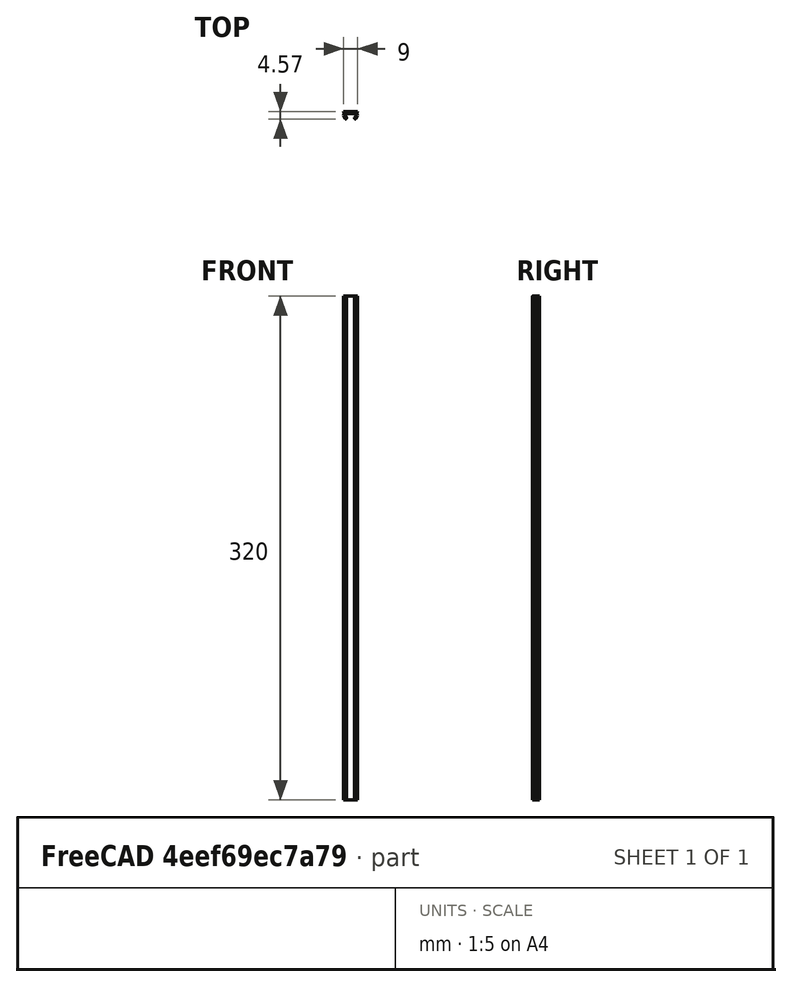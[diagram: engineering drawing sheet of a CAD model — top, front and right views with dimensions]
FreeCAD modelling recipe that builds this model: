
FCSTD DOCUMENT  (FreeCAD 0.17R13387 (Git))
Label: Strip_finishing_channel_8_Y
License: All rights reserved
LicenseURL: http://en.wikipedia.org/wiki/All_rights_reserved
objects: Sketcher::SketchObject×1, PartDesign::Pad×1, PartDesign::Body×1
note: 4 computed .brp shape members not serialized (recipe doc carries the construction recipe); baked Part::Feature solids carry a one-line shape summary decoded from their .brp

FEATURE [Sketcher::SketchObject] Sketch
  MapMode = 5
  Support = -> [XY_Plane]
  sketch-geometry (16):
    g0: LineSegment StartX=-4.5 StartY=4.3 StartZ=0 EndX=4.5 EndY=4.3 EndZ=0
    g1: LineSegment StartX=4.5 StartY=4.3 StartZ=0 EndX=4.5 EndY=4 EndZ=0
    g2: LineSegment StartX=4.5 StartY=4 StartZ=0 EndX=3.9 EndY=4 EndZ=0
    g3: LineSegment StartX=3.9 StartY=4 StartZ=0 EndX=4.5 EndY=2 EndZ=0
    g4: LineSegment StartX=4.5 StartY=2 StartZ=0 EndX=3.44197 EndY=0 EndZ=0
    g5: LineSegment StartX=2.55803 StartY=0.467615 StartZ=0 EndX=3.36869 EndY=2 EndZ=0
    g6: LineSegment StartX=3.36869 StartY=2 StartZ=0 EndX=3 EndY=3.22897 EndZ=0
    g7: LineSegment StartX=-3 StartY=3.22897 StartZ=0 EndX=-3.36869 EndY=2 EndZ=0
    g8: LineSegment StartX=-3.36869 StartY=2 StartZ=0 EndX=-2.55803 EndY=0.467615 EndZ=0
    g9: LineSegment StartX=-3.44197 StartY=0 StartZ=0 EndX=-4.5 EndY=2 EndZ=0
    g10: LineSegment StartX=-4.5 StartY=2 StartZ=0 EndX=-3.9 EndY=4 EndZ=0
    g11: LineSegment StartX=-3.9 StartY=4 StartZ=0 EndX=-4.5 EndY=4 EndZ=0
    g12: LineSegment StartX=-4.5 StartY=4 StartZ=0 EndX=-4.5 EndY=4.3 EndZ=0
    g13: ArcOfCircle CenterX=-3 CenterY=0.233808 CenterZ=0 NormalX=0 NormalY=0 NormalZ=1 AngleXU=0 Radius=0.5 StartAngle=3.62818 EndAngle=6.76978
    g14: ArcOfCircle CenterX=3 CenterY=0.233808 CenterZ=0 NormalX=0 NormalY=0 NormalZ=1 AngleXU=0 Radius=0.5 StartAngle=2.655 EndAngle=5.79659
    g15: LineSegment StartX=-3 StartY=3.22897 StartZ=0 EndX=3 EndY=3.22897 EndZ=0
  constraints (46):
    c: Coincident(g0,g1)
    c: Coincident(g1,g2)
    c: Coincident(g2,g3)
    c: Coincident(g7,g8)
    c: Coincident(g9,g10)
    c: Coincident(g10,g11)
    c: Horizontal(g11)
    c: Coincident(g11,g12)
    c: Coincident(g12,g0)
    c: DistanceX(g0,g0) = 9
    c: Vertical(g12)
    c: Vertical(g1)
    c: Horizontal(g2)
    c: DistanceY(g12,g12) = 0.3
    c: Equal(g12,g1)
    c: Equal(g11,g2)
    c: Symmetric(g0,g0,g-2)
    c: Equal(g9,g4)
    c: Equal(g5,g8)
    c: Parallel(g9,g8)
    c: Parallel(g5,g4)
    c: DistanceX(g2,g2) = 0.6
    c: Coincident(g6,g5)
    c: Coincident(g4,g3)
    c: PointOnObject(g4,g-1)
    c: PointOnObject(g9,g-1)
    c: Symmetric(g9,g4,g-2)
    c: DistanceX(g9,g3) = 9
    c: DistanceY(g0) = 4.3
    c: DistanceY(g3) = 2
    c: Tangent(g13,g8) = 1.5708
    c: Tangent(g13,g9) = 1.5708
    c: Tangent(g14,g4) = 1.5708
    c: Tangent(g14,g5) = 1.5708
    c: Radius(g13) = 0.5
    c: Equal(g13,g14)
    c: Coincident(g15,g7)
    c: Coincident(g15,g6)
    c: Horizontal(g15)
    c: Symmetric(g7,g6,g-2)
    c: Parallel(g10,g7)
    c: Parallel(g6,g3)
    c: DistanceX(g15,g15) = 6
    c: Equal(g7,g6)
    c: DistanceX(g13,g14) = 6
    c: DistanceY(g5) = 2
FEATURE [PartDesign::Pad] Pad
  Length = 320
  Length2 = 100
  Profile = -> Sketch
  Type = 0
FEATURE [PartDesign::Body] Body
  Group = -> [Sketch,Pad]
  Origin = -> Origin
  Tip = -> Pad
